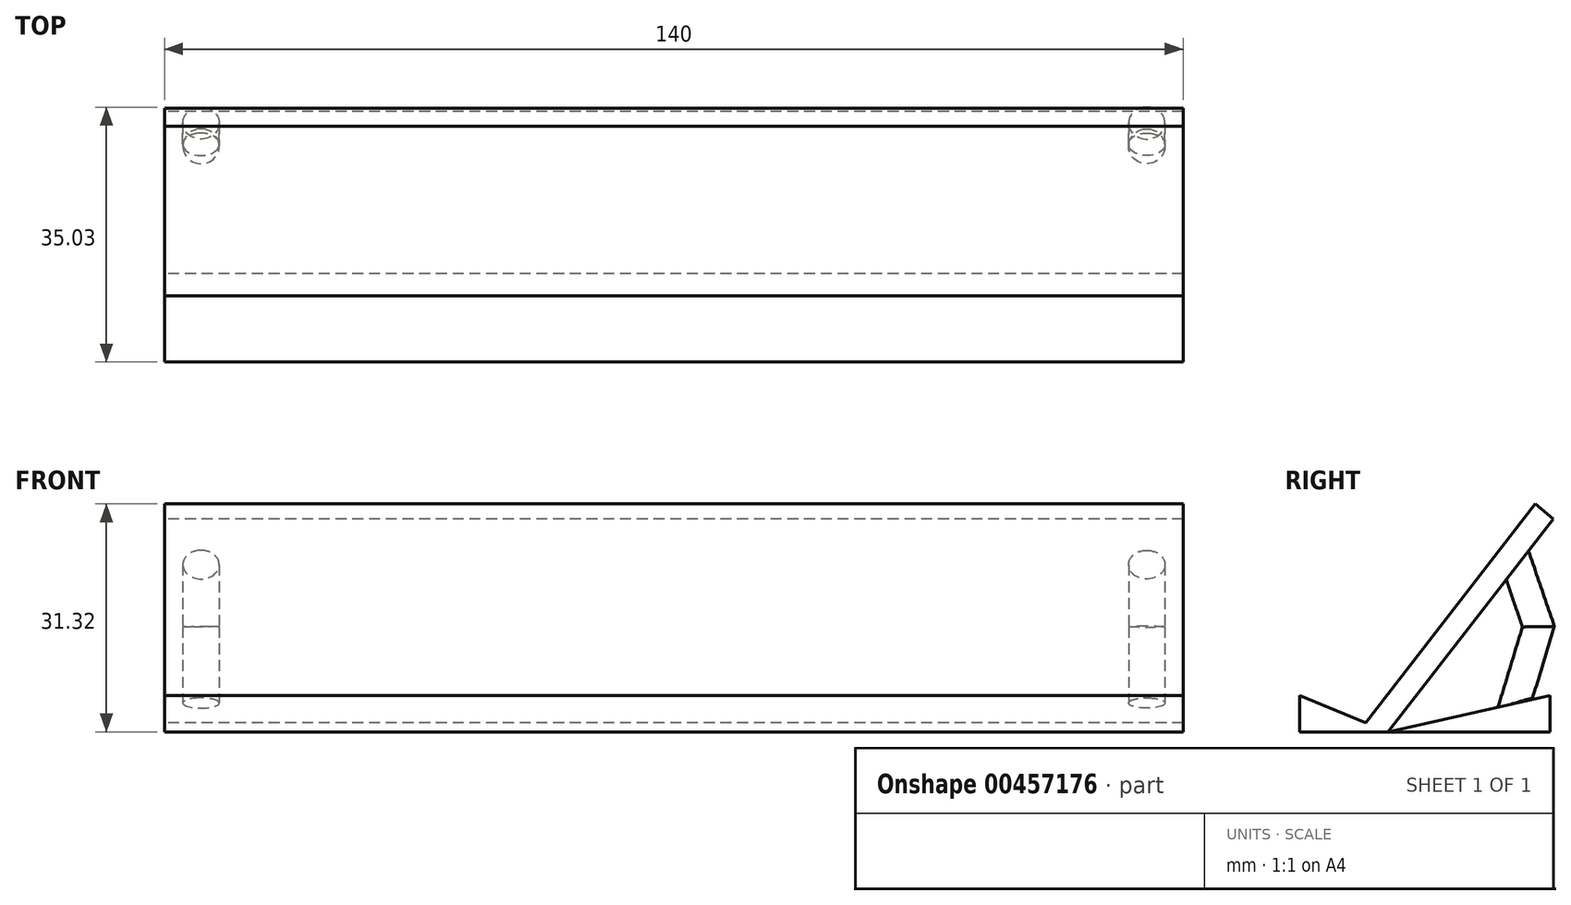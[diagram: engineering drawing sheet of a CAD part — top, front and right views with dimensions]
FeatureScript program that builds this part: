
annotation { "Feature Type Name" : "Feature", "Feature Type Description" : "" }
export const myFeature = defineFeature(function(context is Context, id is Id, definition is map)
    precondition{}
    {
        {
            var Q0;
            Q0=qCreatedBy(makeId("Right.planeOp"),FACE);
            var sketch = newSketch(context, id + "F0", { "sketchPlane" : qUnion([Q0])});
            skLineSegment(sketch, "E0", {"start": v(0, 0) * mm, "end": v(22.7, 29.22) * mm});
            skLineSegment(sketch, "E1", {"start": v(0, 0) * mm, "end": v(-12.15, 5) * mm});
            skLineSegment(sketch, "E2", {"start": v(-12.15, 0) * mm, "end": v(-12.15, 5) * mm});
            skLineSegment(sketch, "E3", {"start": v(-12.15, 0) * mm, "end": v(0, 0) * mm});
            skLineSegment(sketch, "E4", {"start": v(0, 0) * mm, "end": v(22.27, 0) * mm});
            skLineSegment(sketch, "E5", {"start": v(22.27, 0) * mm, "end": v(22.27, 5) * mm});
            skLineSegment(sketch, "E6", {"start": v(22.27, 5) * mm, "end": v(0, 0) * mm});
            skLineSegment(sketch, "E7", {"start": v(20.26, 31.32) * mm, "end": v(22.7, 29.22) * mm});
            skLineSegment(sketch, "E8", {"start": v(20.26, 31.32) * mm, "end": v(-3.08, 1.27) * mm});
            skSolve(sketch);
        }
        {
            var Q0;
            Q0 = qSketchRegion(id + "F0", true);
            extrude(context, id + "F1", {"entities" : qUnion([Q0]), "depth" : 140 * mm});
        }
        {
            var Q0;
            Q0=makeQuery(id+"F1.opExtrude","SWEPT_FACE",FACE,{"disambiguationData":[OSD([sQuery(id+"F0.wireOp",EDGE,"E6")])]});
            var sketch = newSketch(context, id + "F2", { "sketchPlane" : qUnion([Q0])});
            skCircle(sketch, "E9", {"center": v(135, 17.83) * mm, "radius": 2.5 * mm});
            skCircle(sketch, "E10", {"center": v(5, 17.83) * mm, "radius": 2.5 * mm});
            skSolve(sketch);
        }
        {
            var Q0;
            Q0=makeQuery(id+"F1.opExtrude","SWEPT_FACE",FACE,{"disambiguationData":[OSD([sQuery(id+"F0.wireOp",EDGE,"E0")])]});
            var sketch = newSketch(context, id + "F3", { "sketchPlane" : qUnion([Q0])});
            skCircle(sketch, "E11", {"center": v(-135, 29) * mm, "radius": 2.5 * mm});
            skCircle(sketch, "E12", {"center": v(-5, 29) * mm, "radius": 2.5 * mm});
            skSolve(sketch);
        }
        {
            var Q0;
            Q0=makeQuery(id+"F3.imprint","IMPRINT",FACE,{"disambiguationData":[TD([[makeQuery(id+"F3.imprint","IMPRINT",EDGE,{"derivedFrom":sQuery(id+"F3.wireOp",EDGE,"E11")}),1.0]])]});
            var sketch = newSketch(context, id + "F4", { "sketchPlane" : qUnion([Q0])});
            skSolve(sketch);
        }
        {
            var Q0;
            Q0=qCreatedBy(makeId("Right.planeOp"),FACE);
            cPlane(context, id + "F5", {"entities" : qUnion([Q0]), "cplaneType" : CPlaneType.OFFSET, "offset" : 134.9 * mm, "width" : 150 * mm, "height" : 150 * mm});
        }
        {
            var Q0;
            Q0=qCreatedBy(id+"F5.planeOp",FACE);
            var sketch = newSketch(context, id + "F6", { "sketchPlane" : qUnion([Q0])});
            skLineSegment(sketch, "E13", {"start": v(17.69, 22.86) * mm, "end": v(20.57, 14.45) * mm});
            skLineSegment(sketch, "E14", {"start": v(20.57, 14.45) * mm, "end": v(17.37, 3.92) * mm});
            skSolve(sketch);
        }
        {
            var Q0;
            Q0=makeQuery(id+"F3.imprint","IMPRINT",FACE,{"disambiguationData":[TD([[makeQuery(id+"F3.imprint","IMPRINT",EDGE,{"derivedFrom":sQuery(id+"F3.wireOp",EDGE,"E11")}),1.0]])]});
            var Q1;
            Q1=sQuery(id+"F6.wireOp",EDGE,"E13");
            var Q2;
            Q2=sQuery(id+"F6.wireOp",EDGE,"E14");
            sweep(context, id + "F7", {"profiles" : qUnion([Q0]), "path" : qUnion([Q1, Q2])});
        }
        {
            var Q0;
            Q0=qCreatedBy(id+"F5.planeOp",FACE);
            var Q1;
            Q1 = qBodyType(qCreatedBy(id + "F4" ,EDGE), BodyType.WIRE);
            cPlane(context, id + "F8", {"entities" : qUnion([Q0, Q1]), "cplaneType" : CPlaneType.OFFSET, "offset" : 130 * mm, "oppositeDirection" : true, "width" : 150 * mm, "height" : 150 * mm});
        }
        {
            var Q0;
            Q0=qCreatedBy(id+"F8.planeOp",FACE);
            cPlane(context, id + "F9", {"entities" : qUnion([Q0]), "cplaneType" : CPlaneType.OFFSET, "offset" : 65.1 * mm, "width" : 150 * mm, "height" : 150 * mm});
        }
        {
            var Q0;
            Q0=makeQuery(id+"F7.opSweep","SWEPT_BODY",BODY,{"disambiguationData":[OSD([sQuery(id+"F3.wireOp",EDGE,"E11"),sQuery(id+"F6.wireOp",EDGE,"E14")])]});
            var Q1;
            Q1=qCreatedBy(id+"F9.planeOp",FACE);
            mirror(context, id + "F10", {"entities" : qUnion([Q0]), "mirrorPlane" : qUnion([Q1])});
        }
    });
